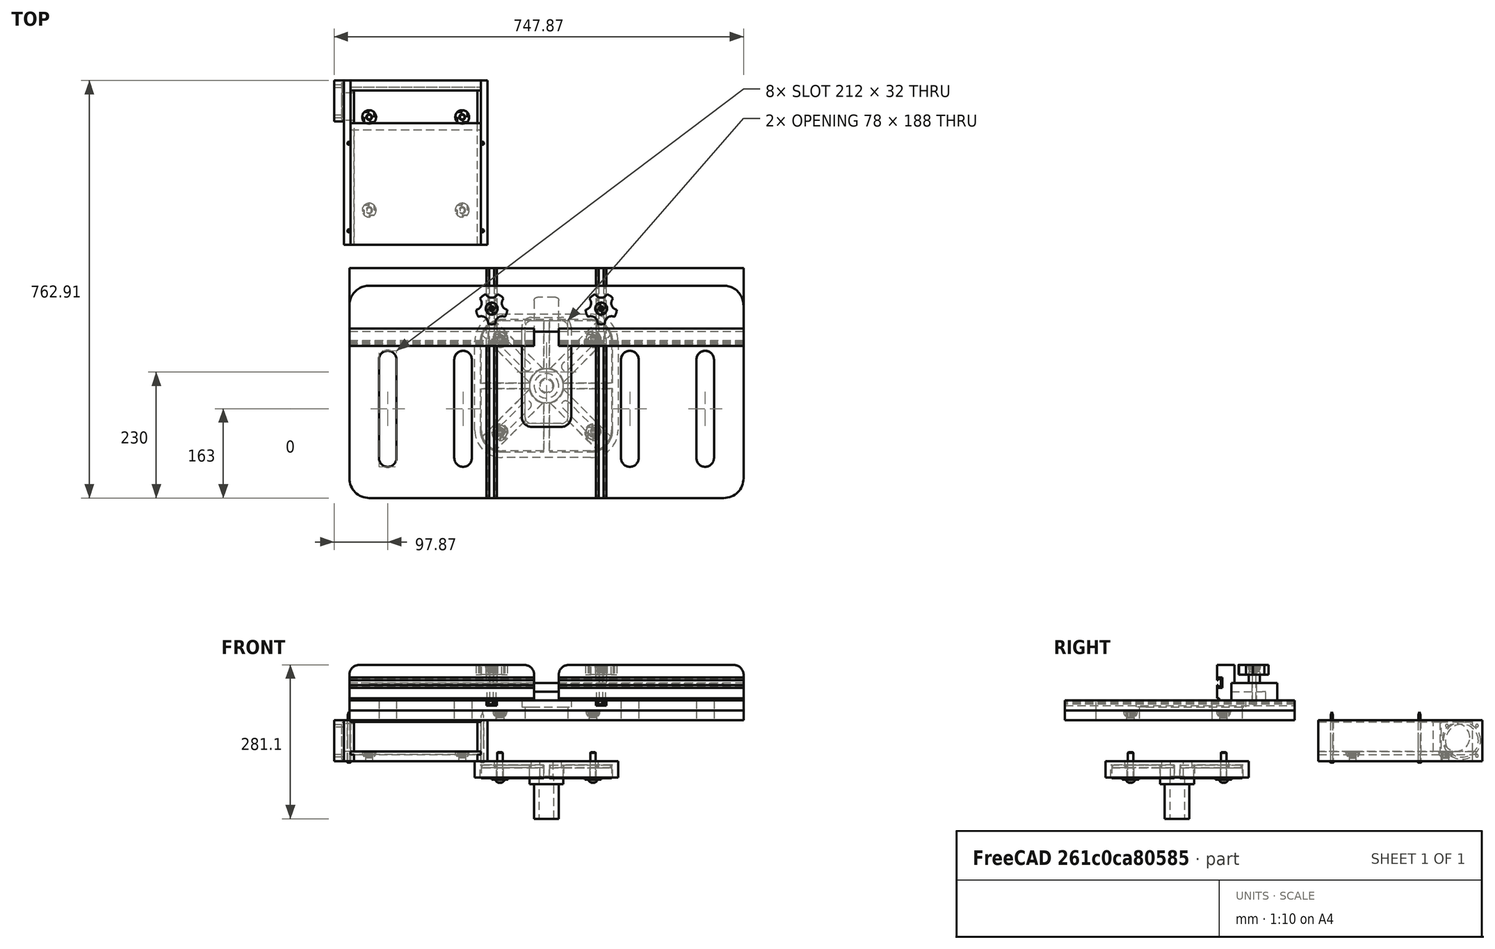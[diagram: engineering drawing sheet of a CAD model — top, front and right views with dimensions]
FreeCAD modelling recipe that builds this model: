
FCSTD DOCUMENT  (FreeCAD 0.22R35466 (Git))
Label: drill_press_table_assembly
License: All rights reserved
LicenseURL: http://en.wikipedia.org/wiki/All_rights_reserved
objects: App::FeaturePython×62, Part::FeaturePython×50, App::DocumentObjectGroup×3, App::Part×1
note: 50 computed .brp shape members not serialized (recipe doc carries the construction recipe); baked Part::Feature solids carry a one-line shape summary decoded from their .brp

FEATURE [Part::FeaturePython] b_drill_press_table_001_  label="drill_press_table_bottom_part_001"  # a2plus imported part (geometry in sourceFile) (typed FeaturePython)
  a2p_Version = 0.4.60n
  fixedPosition = true
  objectType = a2pPart
  sourceFile = ./drill_press_table.FCStd
  sourcePart = bottom_part
  subassemblyImport = false
  timeLastImport = 1.69861e+09
  updateColors = true
FEATURE [Part::FeaturePython] b_drill_press_table_001_001  label="drill_press_table_insert_001"  # a2plus imported part (geometry in sourceFile) (typed FeaturePython)
  Placement = pos=(-1.49495e-06,3.7567e-06,1e-15) rot=(0,0,1;0rad)
  a2p_Version = 0.4.60n
  fixedPosition = false
  objectType = a2pPart
  sourceFile = ./drill_press_table.FCStd
  sourcePart = insert
  subassemblyImport = false
  timeLastImport = 1.69861e+09
  updateColors = true
FEATURE [Part::FeaturePython] b_drill_press_table_001_002  label="drill_press_table_iron_table_001"  # a2plus imported part (geometry in sourceFile) (typed FeaturePython)
  Placement = pos=(0,-5,0) rot=(0,0,1;0rad)
  a2p_Version = 0.4.60n
  fixedPosition = false
  objectType = a2pPart
  sourceFile = ./drill_press_table.FCStd
  sourcePart = iron_table
  subassemblyImport = false
  timeLastImport = 1.69861e+09
  updateColors = true
FEATURE [Part::FeaturePython] b_drill_press_table_001_003  label="drill_press_table_upper_part_001"  # a2plus imported part (geometry in sourceFile) (typed FeaturePython)
  Placement = pos=(4.66166e-07,4.12655e-06,-2e-15) rot=(0,0,1;0rad)
  a2p_Version = 0.4.60n
  fixedPosition = false
  objectType = a2pPart
  sourceFile = ./drill_press_table.FCStd
  sourcePart = upper_part
  subassemblyImport = false
  timeLastImport = 1.69861e+09
  updateColors = true
FEATURE [App::FeaturePython] planeCoincident_001  label="planeCoincident_001__drill_press_table_upper_part_001"  # a2plus constraint (typed FeaturePython)
  Object1 = b_drill_press_table_001_
  Object2 = b_drill_press_table_001_003
  ParentTreeObject = -> b_drill_press_table_001_
  SubElement1 = Face5
  SubElement2 = Face4
  Suppressed = false
  Type = plane
  directionConstraint = 0
  offset = 0
FEATURE [App::FeaturePython] planeCoincident_001_mirror  label="planeCoincident_001__drill_press_table_bottom_part_001"  # a2plus constraint (typed FeaturePython)
  Object1 = b_drill_press_table_001_
  Object2 = b_drill_press_table_001_003
  ParentTreeObject = -> b_drill_press_table_001_003
  SubElement1 = Face5
  SubElement2 = Face4
  Suppressed = false
  Type = plane
  directionConstraint = 0
  offset = 0
FEATURE [App::FeaturePython] axisCoincident_001  label="axisCoincident_001__drill_press_table_bottom_part_001"  # a2plus constraint (typed FeaturePython)
  Object1 = b_drill_press_table_001_003
  Object2 = b_drill_press_table_001_
  ParentTreeObject = -> b_drill_press_table_001_003
  SubElement1 = Edge3
  SubElement2 = Edge4
  Suppressed = false
  Type = axial
  directionConstraint = 0
  lockRotation = false
FEATURE [App::FeaturePython] axisCoincident_001_mirror  label="axisCoincident_001__drill_press_table_upper_part_001"  # a2plus constraint (typed FeaturePython)
  Object1 = b_drill_press_table_001_003
  Object2 = b_drill_press_table_001_
  ParentTreeObject = -> b_drill_press_table_001_
  SubElement1 = Edge3
  SubElement2 = Edge4
  Suppressed = false
  Type = axial
  directionConstraint = 0
  lockRotation = false
FEATURE [App::FeaturePython] axisCoincident_002  label="axisCoincident_002__drill_press_table_bottom_part_001"  # a2plus constraint (typed FeaturePython)
  Object1 = b_drill_press_table_001_003
  Object2 = b_drill_press_table_001_
  ParentTreeObject = -> b_drill_press_table_001_003
  SubElement1 = Edge6
  SubElement2 = Edge7
  Suppressed = false
  Type = axial
  directionConstraint = 0
  lockRotation = false
FEATURE [App::FeaturePython] axisCoincident_002_mirror  label="axisCoincident_002__drill_press_table_upper_part_001"  # a2plus constraint (typed FeaturePython)
  Object1 = b_drill_press_table_001_003
  Object2 = b_drill_press_table_001_
  ParentTreeObject = -> b_drill_press_table_001_
  SubElement1 = Edge6
  SubElement2 = Edge7
  Suppressed = false
  Type = axial
  directionConstraint = 0
  lockRotation = false
FEATURE [Part::FeaturePython] Nut  label="M10-Nut"  # Fasteners workbench fastener (typed FeaturePython)
  Placement = pos=(-85,120,16.9) rot=(1,0,0;3.14159rad)
  baseObject = -> b_drill_press_table_001_ [Edge75]
  diameter = 5
  invert = true
  leftHanded = false
  matchOuter = true
  offset = -1.3
  thread = false
  type = 10
FEATURE [Part::FeaturePython] Nut001  label="M10-Nut007"  # Fasteners workbench fastener (typed FeaturePython)
  Placement = pos=(85,120,16.9) rot=(1,0,0;3.14159rad)
  baseObject = -> b_drill_press_table_001_ [Edge85]
  diameter = 5
  invert = true
  leftHanded = false
  matchOuter = true
  offset = -1.3
  thread = false
  type = 10
FEATURE [Part::FeaturePython] Nut002  label="M10-Nut008"  # Fasteners workbench fastener (typed FeaturePython)
  Placement = pos=(85,290,16.9) rot=(1,0,0;3.14159rad)
  baseObject = -> b_drill_press_table_001_ [Edge105]
  diameter = 5
  invert = true
  leftHanded = false
  matchOuter = true
  offset = -1.3
  thread = false
  type = 10
FEATURE [Part::FeaturePython] Nut003  label="M10-Nut009"  # Fasteners workbench fastener (typed FeaturePython)
  Placement = pos=(-85,290,16.9) rot=(1,0,0;3.14159rad)
  baseObject = -> b_drill_press_table_001_ [Edge95]
  diameter = 5
  invert = true
  leftHanded = false
  matchOuter = true
  offset = -1.3
  thread = false
  type = 10
FEATURE [App::FeaturePython] planeCoincident_002  label="planeCoincident_002__drill_press_table_insert_001"  # a2plus constraint (typed FeaturePython)
  Object1 = b_drill_press_table_001_003
  Object2 = b_drill_press_table_001_001
  ParentTreeObject = -> b_drill_press_table_001_003
  SubElement1 = Face49
  SubElement2 = Face9
  Suppressed = false
  Type = plane
  directionConstraint = 0
  offset = 0
FEATURE [App::FeaturePython] planeCoincident_002_mirror  label="planeCoincident_002__drill_press_table_upper_part_001"  # a2plus constraint (typed FeaturePython)
  Object1 = b_drill_press_table_001_003
  Object2 = b_drill_press_table_001_001
  ParentTreeObject = -> b_drill_press_table_001_001
  SubElement1 = Face49
  SubElement2 = Face9
  Suppressed = false
  Type = plane
  directionConstraint = 0
  offset = 0
FEATURE [App::FeaturePython] axisCoincident_003  label="axisCoincident_003__drill_press_table_upper_part_001"  # a2plus constraint (typed FeaturePython)
  Object1 = b_drill_press_table_001_001
  Object2 = b_drill_press_table_001_003
  ParentTreeObject = -> b_drill_press_table_001_001
  SubElement1 = Edge4
  SubElement2 = Edge86
  Suppressed = false
  Type = axial
  directionConstraint = 0
  lockRotation = false
FEATURE [App::FeaturePython] axisCoincident_003_mirror  label="axisCoincident_003__drill_press_table_insert_001"  # a2plus constraint (typed FeaturePython)
  Object1 = b_drill_press_table_001_001
  Object2 = b_drill_press_table_001_003
  ParentTreeObject = -> b_drill_press_table_001_003
  SubElement1 = Edge4
  SubElement2 = Edge86
  Suppressed = false
  Type = axial
  directionConstraint = 0
  lockRotation = false
FEATURE [App::FeaturePython] axisCoincident_004  label="axisCoincident_004__drill_press_table_upper_part_001"  # a2plus constraint (typed FeaturePython)
  Object1 = b_drill_press_table_001_001
  Object2 = b_drill_press_table_001_003
  ParentTreeObject = -> b_drill_press_table_001_001
  SubElement1 = Edge22
  SubElement2 = Edge88
  Suppressed = false
  Type = axial
  directionConstraint = 0
  lockRotation = false
FEATURE [App::FeaturePython] axisCoincident_004_mirror  label="axisCoincident_004__drill_press_table_insert_001"  # a2plus constraint (typed FeaturePython)
  Object1 = b_drill_press_table_001_001
  Object2 = b_drill_press_table_001_003
  ParentTreeObject = -> b_drill_press_table_001_003
  SubElement1 = Edge22
  SubElement2 = Edge88
  Suppressed = false
  Type = axial
  directionConstraint = 0
  lockRotation = false
FEATURE [Part::FeaturePython] b_drill_press_table_001_004  label="drill_press_table_base_back_001"  # a2plus imported part (geometry in sourceFile) (typed FeaturePython)
  Placement = pos=(-238.868,400.91,1.11091e-08) rot=(0,0,1;0rad)
  a2p_Version = 0.4.60n
  fixedPosition = false
  objectType = a2pPart
  sourceFile = ./drill_press_table.FCStd
  sourcePart = base_back
  subassemblyImport = false
  timeLastImport = 1.69861e+09
  updateColors = true
FEATURE [Part::FeaturePython] b_drill_press_table_001_005  label="drill_press_table_base_bottom_001"  # a2plus imported part (geometry in sourceFile) (typed FeaturePython)
  Placement = pos=(-238.868,400.91,0) rot=(0,0,1;0rad)
  a2p_Version = 0.4.60n
  fixedPosition = false
  objectType = a2pPart
  sourceFile = ./drill_press_table.FCStd
  sourcePart = base_bottom
  subassemblyImport = false
  timeLastImport = 1.69869e+09
  updateColors = true
FEATURE [Part::FeaturePython] b_drill_press_table_001_006  label="drill_press_table_base_divider_001"  # a2plus imported part (geometry in sourceFile) (typed FeaturePython)
  Placement = pos=(-238.868,400.91,1.27725e-08) rot=(0,0,1;0rad)
  a2p_Version = 0.4.60n
  fixedPosition = false
  objectType = a2pPart
  sourceFile = ./drill_press_table.FCStd
  sourcePart = base_divider
  subassemblyImport = false
  timeLastImport = 1.69861e+09
  updateColors = true
FEATURE [Part::FeaturePython] b_drill_press_table_001_007  label="drill_press_table_base_side_left_001"  # a2plus imported part (geometry in sourceFile) (typed FeaturePython)
  Placement = pos=(-238.868,400.91,1.27725e-08) rot=(0,0,1;0rad)
  a2p_Version = 0.4.60n
  fixedPosition = false
  objectType = a2pPart
  sourceFile = ./drill_press_table.FCStd
  sourcePart = base_side_left
  subassemblyImport = false
  timeLastImport = 1.69861e+09
  updateColors = true
FEATURE [Part::FeaturePython] b_drill_press_table_001_008  label="drill_press_table_base_side_right_001"  # a2plus imported part (geometry in sourceFile) (typed FeaturePython)
  Placement = pos=(-238.868,400.91,8.53806e-09) rot=(0,0,1;0rad)
  a2p_Version = 0.4.60n
  fixedPosition = false
  objectType = a2pPart
  sourceFile = ./drill_press_table.FCStd
  sourcePart = base_side_right
  subassemblyImport = false
  timeLastImport = 1.69861e+09
  updateColors = true
FEATURE [Part::FeaturePython] b_drill_press_table_001_009  label="drill_press_table_base_top_001"  # a2plus imported part (geometry in sourceFile) (typed FeaturePython)
  Placement = pos=(-238.868,400.91,1.27725e-08) rot=(0,0,1;0rad)
  a2p_Version = 0.4.60n
  fixedPosition = false
  objectType = a2pPart
  sourceFile = ./drill_press_table.FCStd
  sourcePart = base_top
  subassemblyImport = false
  timeLastImport = 1.69861e+09
  updateColors = true
FEATURE [Part::FeaturePython] b_drill_press_table_001_010  label="drill_press_table_fence_base_001"  # a2plus imported part (geometry in sourceFile) (typed FeaturePython)
  Placement = pos=(2.01055e-06,3.89343,3.52689e-06) rot=(0,0,1;0rad)
  a2p_Version = 0.4.60n
  fixedPosition = false
  objectType = a2pPart
  sourceFile = ./drill_press_table.FCStd
  sourcePart = fence_base
  subassemblyImport = false
  timeLastImport = 1.69861e+09
  updateColors = true
FEATURE [Part::FeaturePython] b_drill_press_table_001_011  label="drill_press_table_fence_face_l_001"  # a2plus imported part (geometry in sourceFile) (typed FeaturePython)
  Placement = pos=(8.99027e-07,3.89343,1.09839e-05) rot=(-0.169513,-0.984562,0.206195;0rad)
  a2p_Version = 0.4.60n
  fixedPosition = false
  objectType = a2pPart
  sourceFile = ./drill_press_table.FCStd
  sourcePart = fence_face_l
  subassemblyImport = false
  timeLastImport = 1.69861e+09
  updateColors = true
FEATURE [Part::FeaturePython] b_drill_press_table_001_012  label="drill_press_table_fence_face_r_001"  # a2plus imported part (geometry in sourceFile) (typed FeaturePython)
  Placement = pos=(5.88635e-06,3.89343,-1.18197e-05) rot=(0.166186,-0.914837,0.790134;0rad)
  a2p_Version = 0.4.60n
  fixedPosition = false
  objectType = a2pPart
  sourceFile = ./drill_press_table.FCStd
  sourcePart = fence_face_r
  subassemblyImport = false
  timeLastImport = 1.69861e+09
  updateColors = true
FEATURE [Part::FeaturePython] b_drill_press_table_001_013  label="drill_press_table_vacuum_port_001"  # a2plus imported part (geometry in sourceFile) (typed FeaturePython)
  Placement = pos=(-238.868,411.399,6.68431e-05) rot=(0,0,1;0rad)
  a2p_Version = 0.4.60n
  fixedPosition = false
  objectType = a2pPart
  sourceFile = ./drill_press_table.FCStd
  sourcePart = vacuum_port
  subassemblyImport = false
  timeLastImport = 1.69861e+09
  updateColors = true
  expr: .Placement.Base.y = 411.36 - 11
FEATURE [App::FeaturePython] planeCoincident_004  label="planeCoincident_004__drill_press_table_upper_part_001"  # a2plus constraint (typed FeaturePython)
  Object1 = b_drill_press_table_001_010
  Object2 = b_drill_press_table_001_003
  ParentTreeObject = -> b_drill_press_table_001_010
  SubElement1 = Face4
  SubElement2 = Face12
  Suppressed = false
  Type = plane
  directionConstraint = 0
  offset = 0
FEATURE [App::FeaturePython] planeCoincident_004_mirror  label="planeCoincident_004__drill_press_table_fence_base_001"  # a2plus constraint (typed FeaturePython)
  Object1 = b_drill_press_table_001_010
  Object2 = b_drill_press_table_001_003
  ParentTreeObject = -> b_drill_press_table_001_003
  SubElement1 = Face4
  SubElement2 = Face12
  Suppressed = false
  Type = plane
  directionConstraint = 0
  offset = 0
FEATURE [App::FeaturePython] axisCoincident_009  label="axisCoincident_009__drill_press_table_upper_part_001"  # a2plus constraint (typed FeaturePython)
  Object1 = b_drill_press_table_001_010
  Object2 = b_drill_press_table_001_003
  ParentTreeObject = -> b_drill_press_table_001_010
  SubElement1 = Edge20
  SubElement2 = Edge4
  Suppressed = false
  Type = axial
  directionConstraint = 0
  lockRotation = false
FEATURE [App::FeaturePython] axisCoincident_009_mirror  label="axisCoincident_009__drill_press_table_fence_base_001"  # a2plus constraint (typed FeaturePython)
  Object1 = b_drill_press_table_001_010
  Object2 = b_drill_press_table_001_003
  ParentTreeObject = -> b_drill_press_table_001_003
  SubElement1 = Edge20
  SubElement2 = Edge4
  Suppressed = false
  Type = axial
  directionConstraint = 0
  lockRotation = false
FEATURE [App::FeaturePython] planeCoincident_005  label="planeCoincident_005__drill_press_table_fence_base_001"  # a2plus constraint (typed FeaturePython)
  Object1 = b_drill_press_table_001_011
  Object2 = b_drill_press_table_001_010
  ParentTreeObject = -> b_drill_press_table_001_011
  SubElement1 = Face4
  SubElement2 = Face3
  Suppressed = false
  Type = plane
  directionConstraint = 0
  offset = 0
FEATURE [App::FeaturePython] planeCoincident_005_mirror  label="planeCoincident_005__drill_press_table_fence_face_l_001"  # a2plus constraint (typed FeaturePython)
  Object1 = b_drill_press_table_001_011
  Object2 = b_drill_press_table_001_010
  ParentTreeObject = -> b_drill_press_table_001_010
  SubElement1 = Face4
  SubElement2 = Face3
  Suppressed = false
  Type = plane
  directionConstraint = 0
  offset = 0
FEATURE [App::FeaturePython] axisCoincident_010  label="axisCoincident_010__drill_press_table_fence_base_001"  # a2plus constraint (typed FeaturePython)
  Object1 = b_drill_press_table_001_011
  Object2 = b_drill_press_table_001_010
  ParentTreeObject = -> b_drill_press_table_001_011
  SubElement1 = Edge21
  SubElement2 = Edge13
  Suppressed = false
  Type = axial
  directionConstraint = 1
  lockRotation = false
FEATURE [App::FeaturePython] axisCoincident_010_mirror  label="axisCoincident_010__drill_press_table_fence_face_l_001"  # a2plus constraint (typed FeaturePython)
  Object1 = b_drill_press_table_001_011
  Object2 = b_drill_press_table_001_010
  ParentTreeObject = -> b_drill_press_table_001_010
  SubElement1 = Edge21
  SubElement2 = Edge13
  Suppressed = false
  Type = axial
  directionConstraint = 1
  lockRotation = false
FEATURE [App::FeaturePython] axisCoincident_011  label="axisCoincident_011__drill_press_table_upper_part_001"  # a2plus constraint (typed FeaturePython)
  Object1 = b_drill_press_table_001_011
  Object2 = b_drill_press_table_001_003
  ParentTreeObject = -> b_drill_press_table_001_011
  SubElement1 = Edge22
  SubElement2 = Edge4
  Suppressed = false
  Type = axial
  directionConstraint = 1
  lockRotation = false
FEATURE [App::FeaturePython] axisCoincident_011_mirror  label="axisCoincident_011__drill_press_table_fence_face_l_001"  # a2plus constraint (typed FeaturePython)
  Object1 = b_drill_press_table_001_011
  Object2 = b_drill_press_table_001_003
  ParentTreeObject = -> b_drill_press_table_001_003
  SubElement1 = Edge22
  SubElement2 = Edge4
  Suppressed = false
  Type = axial
  directionConstraint = 1
  lockRotation = false
FEATURE [App::FeaturePython] planeCoincident_006  label="planeCoincident_006__drill_press_table_fence_base_001"  # a2plus constraint (typed FeaturePython)
  Object1 = b_drill_press_table_001_012
  Object2 = b_drill_press_table_001_010
  ParentTreeObject = -> b_drill_press_table_001_012
  SubElement1 = Face4
  SubElement2 = Face3
  Suppressed = false
  Type = plane
  directionConstraint = 0
  offset = 0
FEATURE [App::FeaturePython] planeCoincident_006_mirror  label="planeCoincident_006__drill_press_table_fence_face_r_001"  # a2plus constraint (typed FeaturePython)
  Object1 = b_drill_press_table_001_012
  Object2 = b_drill_press_table_001_010
  ParentTreeObject = -> b_drill_press_table_001_010
  SubElement1 = Face4
  SubElement2 = Face3
  Suppressed = false
  Type = plane
  directionConstraint = 0
  offset = 0
FEATURE [App::FeaturePython] axisCoincident_012  label="axisCoincident_012__drill_press_table_fence_base_001"  # a2plus constraint (typed FeaturePython)
  Object1 = b_drill_press_table_001_012
  Object2 = b_drill_press_table_001_010
  ParentTreeObject = -> b_drill_press_table_001_012
  SubElement1 = Edge3
  SubElement2 = Edge2
  Suppressed = false
  Type = axial
  directionConstraint = 0
  lockRotation = false
FEATURE [App::FeaturePython] axisCoincident_012_mirror  label="axisCoincident_012__drill_press_table_fence_face_r_001"  # a2plus constraint (typed FeaturePython)
  Object1 = b_drill_press_table_001_012
  Object2 = b_drill_press_table_001_010
  ParentTreeObject = -> b_drill_press_table_001_010
  SubElement1 = Edge3
  SubElement2 = Edge2
  Suppressed = false
  Type = axial
  directionConstraint = 0
  lockRotation = false
FEATURE [App::FeaturePython] axisCoincident_013  label="axisCoincident_013__drill_press_table_upper_part_001"  # a2plus constraint (typed FeaturePython)
  Object1 = b_drill_press_table_001_012
  Object2 = b_drill_press_table_001_003
  ParentTreeObject = -> b_drill_press_table_001_012
  SubElement1 = Edge4
  SubElement2 = Edge66
  Suppressed = false
  Type = axial
  directionConstraint = 0
  lockRotation = false
FEATURE [App::FeaturePython] axisCoincident_013_mirror  label="axisCoincident_013__drill_press_table_fence_face_r_001"  # a2plus constraint (typed FeaturePython)
  Object1 = b_drill_press_table_001_012
  Object2 = b_drill_press_table_001_003
  ParentTreeObject = -> b_drill_press_table_001_003
  SubElement1 = Edge4
  SubElement2 = Edge66
  Suppressed = false
  Type = axial
  directionConstraint = 0
  lockRotation = false
FEATURE [App::FeaturePython] planeCoincident_007  label="planeCoincident_007__drill_press_table_bottom_part_001"  # a2plus constraint (typed FeaturePython)
  Object1 = b_drill_press_table_001_009
  Object2 = b_drill_press_table_001_
  ParentTreeObject = -> b_drill_press_table_001_009
  SubElement1 = Face6
  SubElement2 = Face4
  Suppressed = false
  Type = plane
  directionConstraint = 0
  offset = 0
FEATURE [App::FeaturePython] planeCoincident_007_mirror  label="planeCoincident_007__drill_press_table_base_top_001"  # a2plus constraint (typed FeaturePython)
  Object1 = b_drill_press_table_001_009
  Object2 = b_drill_press_table_001_
  ParentTreeObject = -> b_drill_press_table_001_
  SubElement1 = Face6
  SubElement2 = Face4
  Suppressed = false
  Type = plane
  directionConstraint = 0
  offset = 0
FEATURE [App::FeaturePython] planeCoincident_008  label="planeCoincident_008__drill_press_table_base_top_001"  # a2plus constraint (typed FeaturePython)
  Object1 = b_drill_press_table_001_007
  Object2 = b_drill_press_table_001_009
  ParentTreeObject = -> b_drill_press_table_001_007
  SubElement1 = Face18
  SubElement2 = Face4
  Suppressed = false
  Type = plane
  directionConstraint = 0
  offset = 0
FEATURE [App::FeaturePython] planeCoincident_008_mirror  label="planeCoincident_008__drill_press_table_base_side_left_001"  # a2plus constraint (typed FeaturePython)
  Object1 = b_drill_press_table_001_007
  Object2 = b_drill_press_table_001_009
  ParentTreeObject = -> b_drill_press_table_001_009
  SubElement1 = Face18
  SubElement2 = Face4
  Suppressed = false
  Type = plane
  directionConstraint = 0
  offset = 0
FEATURE [App::FeaturePython] planeCoincident_009  label="planeCoincident_009__drill_press_table_base_top_001"  # a2plus constraint (typed FeaturePython)
  Object1 = b_drill_press_table_001_007
  Object2 = b_drill_press_table_001_009
  ParentTreeObject = -> b_drill_press_table_001_007
  SubElement1 = Face20
  SubElement2 = Face5
  Suppressed = false
  Type = plane
  directionConstraint = 0
  offset = 0
FEATURE [App::FeaturePython] planeCoincident_009_mirror  label="planeCoincident_009__drill_press_table_base_side_left_001"  # a2plus constraint (typed FeaturePython)
  Object1 = b_drill_press_table_001_007
  Object2 = b_drill_press_table_001_009
  ParentTreeObject = -> b_drill_press_table_001_009
  SubElement1 = Face20
  SubElement2 = Face5
  Suppressed = false
  Type = plane
  directionConstraint = 0
  offset = 0
FEATURE [App::FeaturePython] axisCoincident_014  label="axisCoincident_014__drill_press_table_base_side_left_001"  # a2plus constraint (typed FeaturePython)
  Object1 = b_drill_press_table_001_009
  Object2 = b_drill_press_table_001_007
  ParentTreeObject = -> b_drill_press_table_001_009
  SubElement1 = Edge3
  SubElement2 = Edge33
  Suppressed = false
  Type = axial
  directionConstraint = 1
  lockRotation = false
FEATURE [App::FeaturePython] axisCoincident_014_mirror  label="axisCoincident_014__drill_press_table_base_top_001"  # a2plus constraint (typed FeaturePython)
  Object1 = b_drill_press_table_001_009
  Object2 = b_drill_press_table_001_007
  ParentTreeObject = -> b_drill_press_table_001_007
  SubElement1 = Edge3
  SubElement2 = Edge33
  Suppressed = false
  Type = axial
  directionConstraint = 1
  lockRotation = false
FEATURE [App::FeaturePython] planeCoincident_010  label="planeCoincident_010__drill_press_table_base_top_001"  # a2plus constraint (typed FeaturePython)
  Object1 = b_drill_press_table_001_006
  Object2 = b_drill_press_table_001_009
  ParentTreeObject = -> b_drill_press_table_001_006
  SubElement1 = Face1
  SubElement2 = Face5
  Suppressed = false
  Type = plane
  directionConstraint = 0
  offset = 0
FEATURE [App::FeaturePython] planeCoincident_010_mirror  label="planeCoincident_010__drill_press_table_base_divider_001"  # a2plus constraint (typed FeaturePython)
  Object1 = b_drill_press_table_001_006
  Object2 = b_drill_press_table_001_009
  ParentTreeObject = -> b_drill_press_table_001_009
  SubElement1 = Face1
  SubElement2 = Face5
  Suppressed = false
  Type = plane
  directionConstraint = 0
  offset = 0
FEATURE [App::FeaturePython] axisCoincident_015  label="axisCoincident_015__drill_press_table_base_side_left_001"  # a2plus constraint (typed FeaturePython)
  Object1 = b_drill_press_table_001_006
  Object2 = b_drill_press_table_001_007
  ParentTreeObject = -> b_drill_press_table_001_006
  SubElement1 = Edge11
  SubElement2 = Edge68
  Suppressed = false
  Type = axial
  directionConstraint = 1
  lockRotation = false
FEATURE [App::FeaturePython] axisCoincident_015_mirror  label="axisCoincident_015__drill_press_table_base_divider_001"  # a2plus constraint (typed FeaturePython)
  Object1 = b_drill_press_table_001_006
  Object2 = b_drill_press_table_001_007
  ParentTreeObject = -> b_drill_press_table_001_007
  SubElement1 = Edge11
  SubElement2 = Edge68
  Suppressed = false
  Type = axial
  directionConstraint = 1
  lockRotation = false
FEATURE [App::FeaturePython] planeCoincident_011  label="planeCoincident_011__drill_press_table_base_side_left_001"  # a2plus constraint (typed FeaturePython)
  Object1 = b_drill_press_table_001_004
  Object2 = b_drill_press_table_001_007
  ParentTreeObject = -> b_drill_press_table_001_004
  SubElement1 = Face2
  SubElement2 = Face7
  Suppressed = false
  Type = plane
  directionConstraint = 1
  offset = 0
FEATURE [App::FeaturePython] planeCoincident_011_mirror  label="planeCoincident_011__drill_press_table_base_back_001"  # a2plus constraint (typed FeaturePython)
  Object1 = b_drill_press_table_001_004
  Object2 = b_drill_press_table_001_007
  ParentTreeObject = -> b_drill_press_table_001_007
  SubElement1 = Face2
  SubElement2 = Face7
  Suppressed = false
  Type = plane
  directionConstraint = 1
  offset = 0
FEATURE [App::FeaturePython] planeCoincident_012  label="planeCoincident_012__drill_press_table_base_side_left_001"  # a2plus constraint (typed FeaturePython)
  Object1 = b_drill_press_table_001_004
  Object2 = b_drill_press_table_001_007
  ParentTreeObject = -> b_drill_press_table_001_004
  SubElement1 = Face5
  SubElement2 = Face16
  Suppressed = false
  Type = plane
  directionConstraint = 1
  offset = 0
FEATURE [App::FeaturePython] planeCoincident_012_mirror  label="planeCoincident_012__drill_press_table_base_back_001"  # a2plus constraint (typed FeaturePython)
  Object1 = b_drill_press_table_001_004
  Object2 = b_drill_press_table_001_007
  ParentTreeObject = -> b_drill_press_table_001_007
  SubElement1 = Face5
  SubElement2 = Face16
  Suppressed = false
  Type = plane
  directionConstraint = 1
  offset = 0
FEATURE [App::FeaturePython] axisCoincident_016  label="axisCoincident_016__drill_press_table_base_side_left_001"  # a2plus constraint (typed FeaturePython)
  Object1 = b_drill_press_table_001_004
  Object2 = b_drill_press_table_001_007
  ParentTreeObject = -> b_drill_press_table_001_004
  SubElement1 = Edge3
  SubElement2 = Edge7
  Suppressed = false
  Type = axial
  directionConstraint = 0
  lockRotation = false
FEATURE [App::FeaturePython] axisCoincident_016_mirror  label="axisCoincident_016__drill_press_table_base_back_001"  # a2plus constraint (typed FeaturePython)
  Object1 = b_drill_press_table_001_004
  Object2 = b_drill_press_table_001_007
  ParentTreeObject = -> b_drill_press_table_001_007
  SubElement1 = Edge3
  SubElement2 = Edge7
  Suppressed = false
  Type = axial
  directionConstraint = 0
  lockRotation = false
FEATURE [App::FeaturePython] planeCoincident_013  label="planeCoincident_013__drill_press_table_base_back_001"  # a2plus constraint (typed FeaturePython)
  Object1 = b_drill_press_table_001_008
  Object2 = b_drill_press_table_001_004
  ParentTreeObject = -> b_drill_press_table_001_008
  SubElement1 = Face6
  SubElement2 = Face3
  Suppressed = false
  Type = plane
  directionConstraint = 1
  offset = 0
FEATURE [App::FeaturePython] planeCoincident_013_mirror  label="planeCoincident_013__drill_press_table_base_side_right_001"  # a2plus constraint (typed FeaturePython)
  Object1 = b_drill_press_table_001_008
  Object2 = b_drill_press_table_001_004
  ParentTreeObject = -> b_drill_press_table_001_004
  SubElement1 = Face6
  SubElement2 = Face3
  Suppressed = false
  Type = plane
  directionConstraint = 1
  offset = 0
FEATURE [App::FeaturePython] axisCoincident_017  label="axisCoincident_017__drill_press_table_base_back_001"  # a2plus constraint (typed FeaturePython)
  Object1 = b_drill_press_table_001_008
  Object2 = b_drill_press_table_001_004
  ParentTreeObject = -> b_drill_press_table_001_008
  SubElement1 = Edge5
  SubElement2 = Edge12
  Suppressed = false
  Type = axial
  directionConstraint = 1
  lockRotation = false
FEATURE [App::FeaturePython] axisCoincident_017_mirror  label="axisCoincident_017__drill_press_table_base_side_right_001"  # a2plus constraint (typed FeaturePython)
  Object1 = b_drill_press_table_001_008
  Object2 = b_drill_press_table_001_004
  ParentTreeObject = -> b_drill_press_table_001_004
  SubElement1 = Edge5
  SubElement2 = Edge12
  Suppressed = false
  Type = axial
  directionConstraint = 1
  lockRotation = false
FEATURE [App::FeaturePython] axisCoincident_018  label="axisCoincident_018__drill_press_table_base_back_001"  # a2plus constraint (typed FeaturePython)
  Object1 = b_drill_press_table_001_008
  Object2 = b_drill_press_table_001_004
  ParentTreeObject = -> b_drill_press_table_001_008
  SubElement1 = Edge7
  SubElement2 = Edge19
  Suppressed = false
  Type = axial
  directionConstraint = 0
  lockRotation = false
FEATURE [App::FeaturePython] axisCoincident_018_mirror  label="axisCoincident_018__drill_press_table_base_side_right_001"  # a2plus constraint (typed FeaturePython)
  Object1 = b_drill_press_table_001_008
  Object2 = b_drill_press_table_001_004
  ParentTreeObject = -> b_drill_press_table_001_004
  SubElement1 = Edge7
  SubElement2 = Edge19
  Suppressed = false
  Type = axial
  directionConstraint = 0
  lockRotation = false
FEATURE [App::FeaturePython] planeCoincident_014  label="planeCoincident_014__drill_press_table_base_side_left_001"  # a2plus constraint (typed FeaturePython)
  Object1 = b_drill_press_table_001_005
  Object2 = b_drill_press_table_001_007
  ParentTreeObject = -> b_drill_press_table_001_005
  SubElement1 = Face6
  SubElement2 = Face3
  Suppressed = false
  Type = plane
  directionConstraint = 1
  offset = 0
FEATURE [App::FeaturePython] planeCoincident_014_mirror  label="planeCoincident_014__drill_press_table_base_bottom_001"  # a2plus constraint (typed FeaturePython)
  Object1 = b_drill_press_table_001_005
  Object2 = b_drill_press_table_001_007
  ParentTreeObject = -> b_drill_press_table_001_007
  SubElement1 = Face6
  SubElement2 = Face3
  Suppressed = false
  Type = plane
  directionConstraint = 1
  offset = 0
FEATURE [App::FeaturePython] planeCoincident_015  label="planeCoincident_015__drill_press_table_base_back_001"  # a2plus constraint (typed FeaturePython)
  Object1 = b_drill_press_table_001_005
  Object2 = b_drill_press_table_001_004
  ParentTreeObject = -> b_drill_press_table_001_005
  SubElement1 = Face9
  SubElement2 = Face9
  Suppressed = false
  Type = plane
  directionConstraint = 1
  offset = 0
FEATURE [App::FeaturePython] planeCoincident_015_mirror  label="planeCoincident_015__drill_press_table_base_bottom_001"  # a2plus constraint (typed FeaturePython)
  Object1 = b_drill_press_table_001_005
  Object2 = b_drill_press_table_001_004
  ParentTreeObject = -> b_drill_press_table_001_004
  SubElement1 = Face9
  SubElement2 = Face9
  Suppressed = false
  Type = plane
  directionConstraint = 1
  offset = 0
FEATURE [Part::FeaturePython] b_drill_press_table_001_014  label="drill_press_table_iron_table_insert_001"  # a2plus imported part (geometry in sourceFile) (typed FeaturePython)
  Placement = pos=(0,205,-82) rot=(1,0,0;3.14159rad)
  a2p_Version = 0.4.60n
  fixedPosition = false
  objectType = a2pPart
  sourceFile = ./drill_press_table.FCStd
  sourcePart = iron_table_insert
  subassemblyImport = false
  timeLastImport = 1.69861e+09
  updateColors = true
FEATURE [Part::FeaturePython] b_slots_001_001  label="slots_slim_slot_19x9.5x337_001"  # a2plus imported part (geometry in sourceFile) (typed FeaturePython)
  Placement = pos=(-360,287.5,68.5) rot=(0.707107,0,0.707107;3.14159rad)
  a2p_Version = 0.4.60n
  fixedPosition = false
  objectType = a2pPart
  sourceFile = ./slots.FCStd
  sourcePart = slim_slot_19x9.5x337
  subassemblyImport = false
  timeLastImport = 1.69853e+09
  updateColors = true
FEATURE [Part::FeaturePython] b_slots_slim_slot_19x9_5x337_001_  label="slots_slim_slot_19x9.5x337_002"  # a2plus imported part (geometry in sourceFile) (typed FeaturePython)
  Placement = pos=(22.5,287.5,68.5) rot=(0.707107,0,0.707107;3.14159rad)
  a2p_Version = 0.4.60n
  fixedPosition = false
  objectType = a2pPart
  sourceFile = ./slots.FCStd
  sourcePart = slim_slot_19x9.5x337
  subassemblyImport = false
  timeLastImport = 1.69853e+09
  updateColors = true
FEATURE [Part::FeaturePython] b_slots_001_  label="slots_slim_slot_19x9.5x420_001"  # a2plus imported part (geometry in sourceFile) (typed FeaturePython)
  Placement = pos=(-100,420,26.5) rot=(1,0,0;1.5708rad)
  a2p_Version = 0.4.60n
  fixedPosition = false
  objectType = a2pPart
  sourceFile = ./slots.FCStd
  sourcePart = slim_slot_19x9.5x420
  subassemblyImport = false
  timeLastImport = 1.69861e+09
  updateColors = true
  expr: .Placement.Base.z = 36 - 9.5
FEATURE [Part::FeaturePython] b_slots_slim_slot_19x9_5x420_001_  label="slots_slim_slot_19x9.5x420_002"  # a2plus imported part (geometry in sourceFile) (typed FeaturePython)
  Placement = pos=(100,420,26.5) rot=(1,0,0;1.5708rad)
  a2p_Version = 0.4.60n
  fixedPosition = false
  objectType = a2pPart
  sourceFile = ./slots.FCStd
  sourcePart = slim_slot_19x9.5x420
  subassemblyImport = false
  timeLastImport = 1.69861e+09
  updateColors = true
  expr: .Placement.Base.z = 36 - 9.5
FEATURE [Part::FeaturePython] TSlot  label="M6x60-TSlot"  # Fasteners workbench fastener (typed FeaturePython)
  Placement = pos=(100,346,36) rot=(1,0,0;3.14159rad)
  diameter = 2
  invert = true
  leftHanded = false
  length = 5
  lengthCustom = 60
  matchOuter = false
  offset = 0
  slotWidth = 0
  thread = false
  type = 0
FEATURE [Part::FeaturePython] TSlot001  label="M6x60-TSlot001"  # Fasteners workbench fastener (typed FeaturePython)
  Placement = pos=(-100,346,36) rot=(1,0,0;3.14159rad)
  diameter = 2
  invert = true
  leftHanded = false
  length = 5
  lengthCustom = 60
  matchOuter = false
  offset = 0
  slotWidth = 0
  thread = false
  type = 0
FEATURE [Part::FeaturePython] b_knob_5_001_  label="knob_5_knob_001"  # a2plus imported part (geometry in sourceFile) (typed FeaturePython)
  Placement = pos=(100,346,83) rot=(0,0,1;0rad)
  a2p_Version = 0.4.60n
  fixedPosition = false
  objectType = a2pPart
  sourceFile = ./../knob_5.FCStd
  sourcePart = knob
  subassemblyImport = false
  timeLastImport = 1698515087
  updateColors = true
FEATURE [Part::FeaturePython] b_knob_5_001_001  label="knob_5_plug_001"  # a2plus imported part (geometry in sourceFile) (typed FeaturePython)
  Placement = pos=(100,346,81) rot=(0,0,1;0rad)
  a2p_Version = 0.4.60n
  fixedPosition = false
  objectType = a2pPart
  sourceFile = ./../knob_5.FCStd
  sourcePart = plug
  subassemblyImport = false
  timeLastImport = 1698515087
  updateColors = true
FEATURE [Part::FeaturePython] b_knob_5_knob_001_  label="knob_5_knob_002"  # a2plus imported part (geometry in sourceFile) (typed FeaturePython)
  Placement = pos=(-100,346,83) rot=(0,0,1;0rad)
  a2p_Version = 0.4.60n
  fixedPosition = false
  objectType = a2pPart
  sourceFile = ./../knob_5.FCStd
  sourcePart = knob
  subassemblyImport = false
  timeLastImport = 1698515087
  updateColors = true
FEATURE [Part::FeaturePython] b_knob_5_plug_001_  label="knob_5_plug_002"  # a2plus imported part (geometry in sourceFile) (typed FeaturePython)
  Placement = pos=(-100,346,81) rot=(0,0,1;0rad)
  a2p_Version = 0.4.60n
  fixedPosition = false
  objectType = a2pPart
  sourceFile = ./../knob_5.FCStd
  sourcePart = plug
  subassemblyImport = false
  timeLastImport = 1698515087
  updateColors = true
FEATURE [App::FeaturePython] axisCoincident_005  label="axisCoincident_005__drill_press_table_base_side_left_001"  # a2plus constraint (typed FeaturePython)
  Object1 = b_drill_press_table_001_005
  Object2 = b_drill_press_table_001_007
  ParentTreeObject = -> b_drill_press_table_001_005
  SubElement1 = Edge24
  SubElement2 = Edge36
  Suppressed = false
  Type = axial
  directionConstraint = 0
  lockRotation = false
FEATURE [App::FeaturePython] axisCoincident_005_mirror  label="axisCoincident_005__drill_press_table_base_bottom_001"  # a2plus constraint (typed FeaturePython)
  Object1 = b_drill_press_table_001_005
  Object2 = b_drill_press_table_001_007
  ParentTreeObject = -> b_drill_press_table_001_007
  SubElement1 = Edge24
  SubElement2 = Edge36
  Suppressed = false
  Type = axial
  directionConstraint = 0
  lockRotation = false
FEATURE [App::FeaturePython] planesParallel_001  label="planesParallel_001__drill_press_table_base_side_left_001"  # a2plus constraint (typed FeaturePython)
  Object1 = b_drill_press_table_001_005
  Object2 = b_drill_press_table_001_007
  ParentTreeObject = -> b_drill_press_table_001_005
  SubElement1 = Face7
  SubElement2 = Face17
  Suppressed = false
  Type = planesParallel
  directionConstraint = 1
FEATURE [App::FeaturePython] planesParallel_001_mirror  label="planesParallel_001__drill_press_table_base_bottom_001"  # a2plus constraint (typed FeaturePython)
  Object1 = b_drill_press_table_001_005
  Object2 = b_drill_press_table_001_007
  ParentTreeObject = -> b_drill_press_table_001_007
  SubElement1 = Face7
  SubElement2 = Face17
  Suppressed = false
  Type = planesParallel
  directionConstraint = 1
FEATURE [App::FeaturePython] planeCoincident_003  label="planeCoincident_003__drill_press_table_base_side_left_001"  # a2plus constraint (typed FeaturePython)
  Object1 = b_drill_press_table_001_005
  Object2 = b_drill_press_table_001_007
  ParentTreeObject = -> b_drill_press_table_001_005
  SubElement1 = Face7
  SubElement2 = Face17
  Suppressed = false
  Type = plane
  directionConstraint = 1
  offset = 1
FEATURE [App::FeaturePython] planeCoincident_003_mirror  label="planeCoincident_003__drill_press_table_base_bottom_001"  # a2plus constraint (typed FeaturePython)
  Object1 = b_drill_press_table_001_005
  Object2 = b_drill_press_table_001_007
  ParentTreeObject = -> b_drill_press_table_001_007
  SubElement1 = Face7
  SubElement2 = Face17
  Suppressed = false
  Type = plane
  directionConstraint = 1
  offset = 1
FEATURE [Part::FeaturePython] b_drill_press_table_iron_table_insert_001_  label="drill_press_table_iron_table_insert_002"  # a2plus imported part (geometry in sourceFile) (typed FeaturePython)
  Placement = pos=(0,205,-82) rot=(0.707107,0.707107,0;3.14159rad)
  a2p_Version = 0.4.60n
  fixedPosition = false
  objectType = a2pPart
  sourceFile = ./drill_press_table.FCStd
  sourcePart = iron_table_insert
  subassemblyImport = false
  timeLastImport = 1.69861e+09
  updateColors = true
FEATURE [Part::FeaturePython] b_drill_press_table_iron_table_insert_001_001  label="drill_press_table_iron_table_insert_003"  # a2plus imported part (geometry in sourceFile) (typed FeaturePython)
  Placement = pos=(0,205,-82) rot=(0.707107,-0.707107,0;3.14159rad)
  a2p_Version = 0.4.60n
  fixedPosition = false
  objectType = a2pPart
  sourceFile = ./drill_press_table.FCStd
  sourcePart = iron_table_insert
  subassemblyImport = false
  timeLastImport = 1.69861e+09
  updateColors = true
FEATURE [Part::FeaturePython] b_drill_press_table_iron_table_insert_001_002  label="drill_press_table_iron_table_insert_004"  # a2plus imported part (geometry in sourceFile) (typed FeaturePython)
  Placement = pos=(0,205,-82) rot=(0,1,0;3.14159rad)
  a2p_Version = 0.4.60n
  fixedPosition = false
  objectType = a2pPart
  sourceFile = ./drill_press_table.FCStd
  sourcePart = iron_table_insert
  subassemblyImport = false
  timeLastImport = 1.69861e+09
  updateColors = true
FEATURE [Part::FeaturePython] Washer  label="M10-Washer"  # Fasteners workbench fastener (typed FeaturePython)
  Placement = pos=(-85,120,-106) rot=(1,0,0;3.14159rad)
  baseObject = -> b_drill_press_table_iron_table_insert_001_001 [Edge20]
  diameter = 7
  invert = false
  matchOuter = false
  offset = 0
  type = 8
FEATURE [Part::FeaturePython] Washer001  label="M10-Washer004"  # Fasteners workbench fastener (typed FeaturePython)
  Placement = pos=(85,120,-106) rot=(1,0,0;3.14159rad)
  baseObject = -> b_drill_press_table_001_014 [Edge20]
  diameter = 7
  invert = false
  matchOuter = false
  offset = 0
  type = 8
FEATURE [Part::FeaturePython] Washer002  label="M10-Washer005"  # Fasteners workbench fastener (typed FeaturePython)
  Placement = pos=(-85,290,-106) rot=(1,0,0;3.14159rad)
  baseObject = -> b_drill_press_table_iron_table_insert_001_002 [Edge20]
  diameter = 7
  invert = false
  matchOuter = false
  offset = 0
  type = 8
FEATURE [Part::FeaturePython] Washer003  label="M10-Washer006"  # Fasteners workbench fastener (typed FeaturePython)
  Placement = pos=(85,290,-106) rot=(1,0,0;3.14159rad)
  baseObject = -> b_drill_press_table_iron_table_insert_001_ [Edge20]
  diameter = 7
  invert = false
  matchOuter = false
  offset = 0
  type = 8
FEATURE [Part::FeaturePython] Screw  label="M10x50-Screw"  # Fasteners workbench fastener (typed FeaturePython)
  Placement = pos=(85,290,-108.5) rot=(1,0,0;3.14159rad)
  baseObject = -> Washer003 [Edge1]
  diameter = 6
  invert = false
  leftHanded = false
  length = 7
  lengthCustom = 50
  matchOuter = false
  offset = 0
  thread = false
  type = 54
FEATURE [Part::FeaturePython] Screw001  label="M10x50-Screw006"  # Fasteners workbench fastener (typed FeaturePython)
  Placement = pos=(85,120,-108.5) rot=(1,0,0;3.14159rad)
  baseObject = -> Washer001 [Edge1]
  diameter = 6
  invert = false
  leftHanded = false
  length = 7
  lengthCustom = 50
  matchOuter = false
  offset = 0
  thread = false
  type = 54
FEATURE [Part::FeaturePython] Screw002  label="M10x50-Screw007"  # Fasteners workbench fastener (typed FeaturePython)
  Placement = pos=(-85,120,-108.5) rot=(1,0,0;3.14159rad)
  baseObject = -> Washer [Edge1]
  diameter = 6
  invert = false
  leftHanded = false
  length = 7
  lengthCustom = 50
  matchOuter = false
  offset = 0
  thread = false
  type = 54
FEATURE [Part::FeaturePython] Screw003  label="M10x50-Screw008"  # Fasteners workbench fastener (typed FeaturePython)
  Placement = pos=(-85,290,-108.5) rot=(1,0,0;3.14159rad)
  baseObject = -> Washer002 [Edge1]
  diameter = 6
  invert = false
  leftHanded = false
  length = 7
  lengthCustom = 50
  matchOuter = false
  offset = 0
  thread = false
  type = 54
FEATURE [App::DocumentObjectGroup] Group  label="iron_table_inserts"
  Group = -> [b_drill_press_table_iron_table_insert_001_,b_drill_press_table_001_014,b_drill_press_table_iron_table_insert_001_001,b_drill_press_table_iron_table_insert_001_002,Washer,Washer001,Washer002,Washer003,Screw,Screw001,Screw002,Screw003]
FEATURE [Part::FeaturePython] Nut004  label="M10-Nut018"  # Fasteners workbench fastener (typed FeaturePython)
  Placement = pos=(-153.87,526,-57) rot=(1,0,0;3.14159rad)
  diameter = 5
  invert = true
  leftHanded = false
  matchOuter = false
  offset = 0
  thread = false
  type = 10
FEATURE [Part::FeaturePython] Nut005  label="M10-Nut019"  # Fasteners workbench fastener (typed FeaturePython)
  Placement = pos=(-323.87,526,-57) rot=(1,0,0;3.14159rad)
  diameter = 5
  invert = true
  leftHanded = false
  matchOuter = false
  offset = 0
  thread = false
  type = 10
FEATURE [Part::FeaturePython] Nut006  label="M10-Nut020"  # Fasteners workbench fastener (typed FeaturePython)
  Placement = pos=(-153.87,696,-57) rot=(1,0,0;3.14159rad)
  diameter = 5
  invert = true
  leftHanded = false
  matchOuter = false
  offset = 0
  thread = false
  type = 10
FEATURE [Part::FeaturePython] Nut007  label="M10-Nut021"  # Fasteners workbench fastener (typed FeaturePython)
  Placement = pos=(-323.87,696,-57) rot=(1,0,0;3.14159rad)
  diameter = 5
  invert = true
  leftHanded = false
  matchOuter = false
  offset = 0
  thread = false
  type = 10
FEATURE [App::DocumentObjectGroup] Group001  label="table"
  Group = -> [b_drill_press_table_001_,b_drill_press_table_001_001,b_drill_press_table_001_003,Nut,Nut001,Nut002,Nut003]
FEATURE [Part::FeaturePython] Screw004  label="4 mmx90-Screw"  # Fasteners workbench fastener (typed FeaturePython)
  Placement = pos=(-116.868,487.91,-75) rot=(1,0,0;3.14159rad)
  baseObject = -> b_drill_press_table_001_008 [Edge29]
  diameter = 5
  invert = true
  leftHanded = false
  length = 11
  lengthCustom = 90
  matchOuter = false
  offset = 0
  thread = false
  type = 20
FEATURE [Part::FeaturePython] Screw005  label="4 mmx90-Screw001"  # Fasteners workbench fastener (typed FeaturePython)
  Placement = pos=(-360.868,487.91,-75) rot=(1,0,0;3.14159rad)
  baseObject = -> b_drill_press_table_001_007 [Edge17]
  diameter = 5
  invert = true
  leftHanded = false
  length = 11
  lengthCustom = 90
  matchOuter = false
  offset = 0
  thread = false
  type = 20
FEATURE [Part::FeaturePython] Screw006  label="4 mmx90-Screw002"  # Fasteners workbench fastener (typed FeaturePython)
  Placement = pos=(-116.868,647.91,-75) rot=(1,0,0;3.14159rad)
  baseObject = -> b_drill_press_table_001_008 [Edge30]
  diameter = 5
  invert = true
  leftHanded = false
  length = 11
  lengthCustom = 90
  matchOuter = false
  offset = 0
  thread = false
  type = 20
FEATURE [Part::FeaturePython] Screw007  label="4 mmx90-Screw003"  # Fasteners workbench fastener (typed FeaturePython)
  Placement = pos=(-360.868,647.91,-75) rot=(1,0,0;3.14159rad)
  baseObject = -> b_drill_press_table_001_007 [Edge16]
  diameter = 5
  invert = true
  leftHanded = false
  length = 11
  lengthCustom = 90
  matchOuter = false
  offset = 0
  thread = false
  type = 20
FEATURE [App::Part] Part  label="base"
  Group = -> [planeCoincident_012,axisCoincident_018_mirror,axisCoincident_017_mirror,planeCoincident_011,planeCoincident_015_mirror,axisCoincident_016,planeCoincident_013_mirror,b_drill_press_table_001_004,planeCoincident_015,planeCoincident_014,b_drill_press_table_001_005,planeCoincident_010,axisCoincident_015,b_drill_press_table_001_006,planeCoincident_009,planeCoincident_008,axisCoincident_016_mirror,+25 more]
  Origin = -> Origin
  Placement = pos=(238.87,-406,0) rot=(0,0,1;0rad)
FEATURE [Part::FeaturePython] Nut008  label="M8-Nut"  # Fasteners workbench fastener (typed FeaturePython)
  Placement = pos=(-100,346,97.5) rot=(1,0,0;3.14159rad)
  baseObject = -> b_knob_5_knob_001_ [Edge38]
  diameter = 4
  invert = true
  leftHanded = false
  matchOuter = false
  offset = -1.5
  thread = false
  type = 10
FEATURE [Part::FeaturePython] Nut009  label="M8-Nut001"  # Fasteners workbench fastener (typed FeaturePython)
  Placement = pos=(100,346,97.5) rot=(1,0,0;3.14159rad)
  baseObject = -> b_knob_5_001_ [Edge38]
  diameter = 4
  invert = true
  leftHanded = false
  matchOuter = false
  offset = -1.5
  thread = false
  type = 10
FEATURE [App::DocumentObjectGroup] Group002  label="fences"
  Group = -> [b_drill_press_table_001_010,b_drill_press_table_001_011,b_drill_press_table_001_012,b_slots_001_001,b_slots_slim_slot_19x9_5x337_001_,b_slots_001_,b_slots_slim_slot_19x9_5x420_001_,TSlot,TSlot001,b_knob_5_001_,b_knob_5_001_001,b_knob_5_knob_001_,b_knob_5_plug_001_,Nut008,Nut009]
